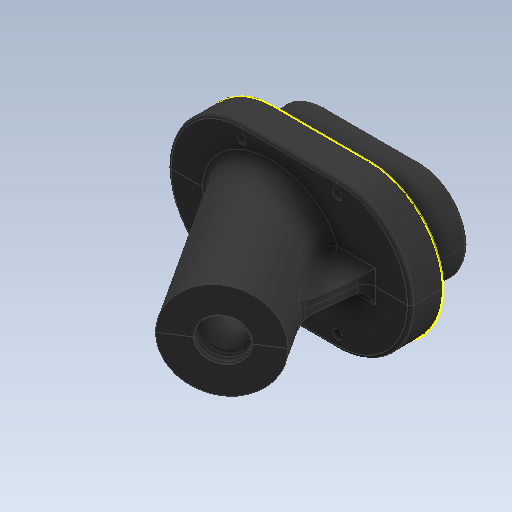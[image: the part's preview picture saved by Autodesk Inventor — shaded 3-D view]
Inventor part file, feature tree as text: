
AUTODESK INVENTOR PART (.ipt)
format: ipt  version: 2020 (Build 240168000, 168)  size: 872,960 bytes
history: native  units: mm
features: sketch x10, extrude x8, projected_geometry x5, other x5, fillet x4, reference x4, move_body x2, plane x1, split x1, direct_edit x1, hole x1, sweep x1
ambient origin geometry x8: Origin, YZ Plane, XZ Plane, XY Plane, X Axis, Y Axis, Z Axis, Center Point
bodies: Solid1 (feature_tree), Solid2 (feature_tree), Solid3 (feature_tree)
feature tree (43):
  sketch  "Sketch1"  dims[d0=16.0mm d1=0.0mm d2=10.0mm d3=0.0mm]
  extrude  "Extrusion1"  Depth=10.0mm TaperAngle=0.0deg
  extrude  "Extrusion2"  Depth=30.0mm
  plane  "Work Plane3"
  extrude  "Extrusion3"  Depth=20.0mm
  extrude  "Extrusion4"  Depth=1.0mm
  fillet  "Fillet1"  Radius=4.0mm
  split  "Split1"
  extrude  "Extrusion5"  Depth=0.1mm
  direct_edit  "Direct Edit1"
  extrude  "Extrusion6"  TaperAngle=0.0deg  [1 undecoded]
  extrude  "Extrusion7"  TaperAngle=0.0deg  [1 undecoded]
  extrude  "Extrusion8"  Depth=30.0mm TaperAngle=0.0deg
  hole  "Hole1"  [1 undecoded]
  sweep  "Sweep1"
  fillet  "Fillet2"  Radius=12.2mm
  fillet  "Fillet3"  Radius=0.5mm
  fillet  "Fillet4"  Radius=0.5mm
  reference  "Reference1"
  sketch  "Sketch4"  dims[d4=8.0mm d5=30.0mm]
  sketch  "Sketch5"  dims[d6=50.0mm d7=8.0mm d8=0.0mm d9=0.0mm d10=20.0mm]
  projected_geometry  "Projected Loop1"
  projected_geometry  "Projected Loop2"
  projected_geometry  "Projected Loop3"
  sketch  "Sketch6"  dims[d11=6.981317mm d12=1.0mm d13=4.0mm d14=0.0mm]
  reference  "Reference2"
  reference  "Reference3"
  reference  "Reference4"
  sketch  "Sketch7"  dims[d15=3.0mm d16=0.1mm]
  sketch  "Sketch8"  dims[d17=25.4mm d18=0.0mm d19=0.0mm d20=0.0mm d21=-8.25mm]
  sketch  "Sketch9"  dims[d22=10.0mm d23=0.0mm d24=0.0mm d25=0.0mm d26=-10.75mm]
  sketch  "Sketch10"  dims[d27=12.7mm d28=30.0mm d29=0.0mm]
  projected_geometry  "Projected Loop4"
  projected_geometry  "Projected Loop5"
  sketch  "Sketch11"  dims[d30=12.2mm d31=0.5mm d32=10.0mm d33=12.2mm d34=0.0mm d35=3.0mm d36=6.0mm d37=4.0mm d38=2.0mm d39=90.0deg d40=8.0mm d41=20.594885mm d42=0.5mm d43=0.5mm d44=0.5mm d45=0.5mm d46=0.5mm d47=0.1mm d48=1.0mm d49=0.5mm d50=1.5mm d51=40.0mm d52=12.7mm d53=0.0mm d54=0.0mm d55=0.0mm d56=0.1mm d57=1.0mm d58=1.0mm]
  sketch  "3D Sketch1"
  other  "Helical Curve1"
  other  "<userpath>\Documents\GitHub\OpenRaman\Hardware\OpenRaman.V1.iam"
  other  "OpenRaman.V1.iam"
  other  "SpectometerTube:1"
  other  "PrismsGeometry:1"
  move_body  "Move1"
  move_body  "Move2"
note: 3 required parameter values undecoded (feature->parameter linkage not recoverable at this tier; creation-order binding heuristic only, values carry confidence <= 0.55)
